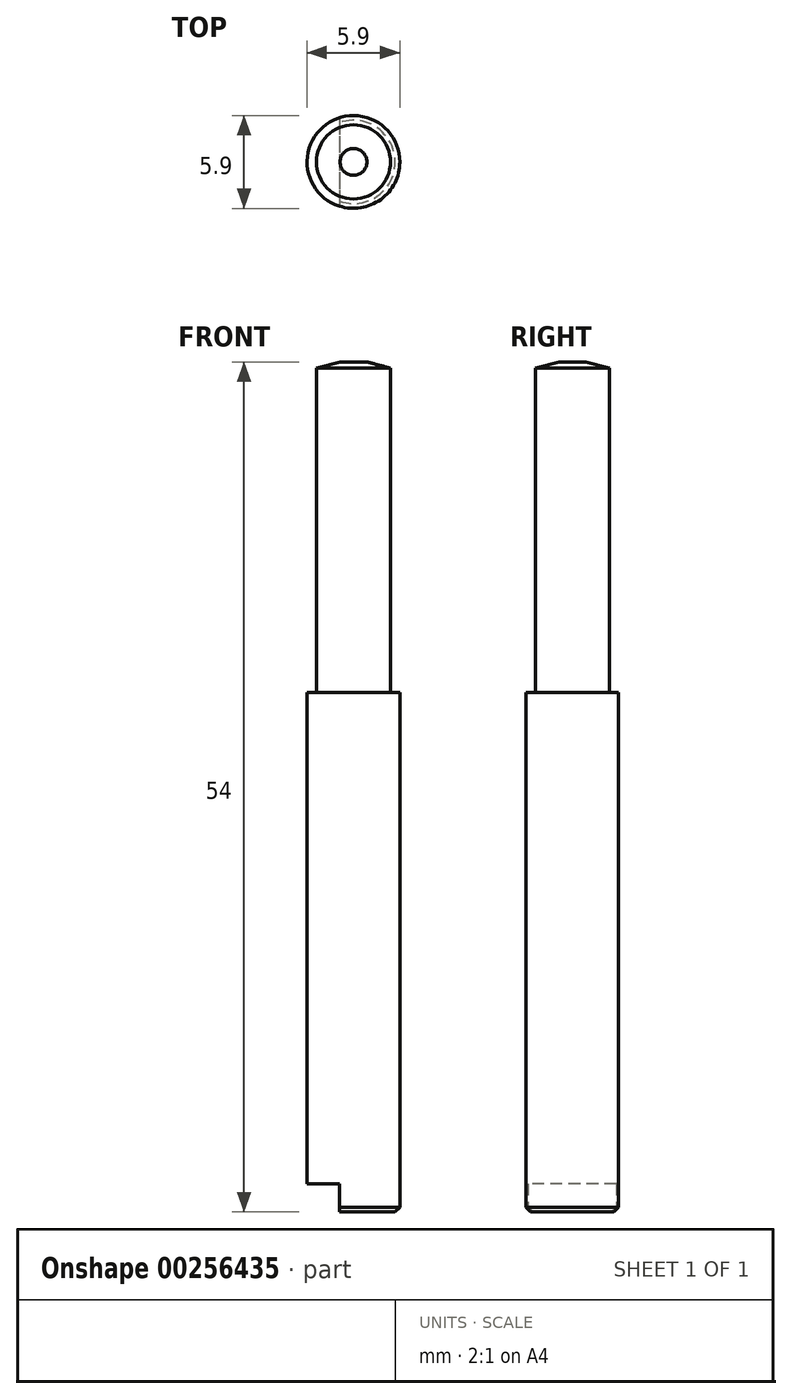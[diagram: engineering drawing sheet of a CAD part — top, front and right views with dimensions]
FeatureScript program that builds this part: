
annotation { "Feature Type Name" : "Feature", "Feature Type Description" : "" }
export const myFeature = defineFeature(function(context is Context, id is Id, definition is map)
    precondition{}
    {
        {
            var Q0;
            Q0=qCreatedBy(makeId("Top.planeOp"),FACE);
            var sketch = newSketch(context, id + "F0", { "sketchPlane" : qUnion([Q0])});
            skCircle(sketch, "E0", {"center": v(0, 0) * mm, "radius": 0.98 * mm});
            skSolve(sketch);
        }
        {
            var Q0;
            Q0=qSketchRegion(id+"F0",true);
            extrude(context, id + "F1", {"entities" : qUnion([Q0]), "depth" : 11 * mm});
        }
        {
            var Q0;
            Q0=makeQuery(id+"F1.opExtrude","CAP_FACE",FACE,{"disambiguationData":[OSD([sQuery(id+"F0.wireOp",EDGE,"E0")])],"isStart":false});
            var sketch = newSketch(context, id + "F2", { "sketchPlane" : qUnion([Q0])});
            skCircle(sketch, "E1", {"center": v(0, 0) * mm, "radius": 0.78 * mm});
            skSolve(sketch);
        }
        {
            var Q0;
            Q0=qSketchRegion(id+"F2",true);
            extrude(context, id + "F3", {"entities" : qUnion([Q0]), "operationType" : NewBodyOperationType.ADD, "depth" : 7 * mm});
        }
        {
            var Q0;
            Q0=makeQuery(id+"F1.opExtrude","CAP_EDGE",EDGE,{"disambiguationData":[OSD([sQuery(id+"F0.wireOp",EDGE,"E0")])],"isStart":true});
            chamfer(context, id + "F4", {"entities" : qUnion([Q0]), "width" : 0.1 * mm, "tangentPropagation" : true});
        }
        {
            var Q0;
            Q0=makeQuery(id+"F3.opExtrude","CAP_EDGE",EDGE,{"disambiguationData":[OSD([sQuery(id+"F2.wireOp",EDGE,"E1")])],"isStart":false});
            chamfer(context, id + "F5", {"entities" : qUnion([Q0]), "chamferType" : ChamferType.OFFSET_ANGLE, "width" : 0.5 * mm, "oppositeDirection" : true, "angle" : 15 * degree, "tangentPropagation" : true});
        }
        {
            var Q0;
            Q0=qCreatedBy(makeId("Front.planeOp"),FACE);
            var sketch = newSketch(context, id + "F6", { "sketchPlane" : qUnion([Q0])});
            skLineSegment(sketch, "E2.bottom", {"start": v(-0.3, 0) * mm, "end": v(-1, 0) * mm});
            skLineSegment(sketch, "E2.top", {"start": v(-0.3, 0.6) * mm, "end": v(-1, 0.6) * mm});
            skLineSegment(sketch, "E2.left", {"start": v(-0.3, 0) * mm, "end": v(-0.3, 0.6) * mm});
            skLineSegment(sketch, "E2.right", {"start": v(-1, 0) * mm, "end": v(-1, 0.6) * mm});
            skSolve(sketch);
        }
        {
            var Q0;
            Q0=qSketchRegion(id+"F6",true);
            extrude(context, id + "F7", {"entities" : qUnion([Q0]), "operationType" : NewBodyOperationType.REMOVE, "oppositeDirection" : true, "depth" : 2 * mm, "symmetric" : true});
        }
        {
            var Q0;
            Q0=makeQuery(id+"F1.opExtrude","SWEPT_BODY",BODY,{"disambiguationData":[OSD([sQuery(id+"F0.wireOp",EDGE,"E0")])]});
            var Q1;
            Q1=qCreatedBy(makeId("Origin.pointOp"),VERTEX);
            transform(context, id + "F8", {"entities" : qUnion([Q0]), "transformType" : TransformType.SCALE_UNIFORMLY, "scale" : 3, "makeCopy" : false, "scalePoint" : qUnion([Q1])});
        }
    });
